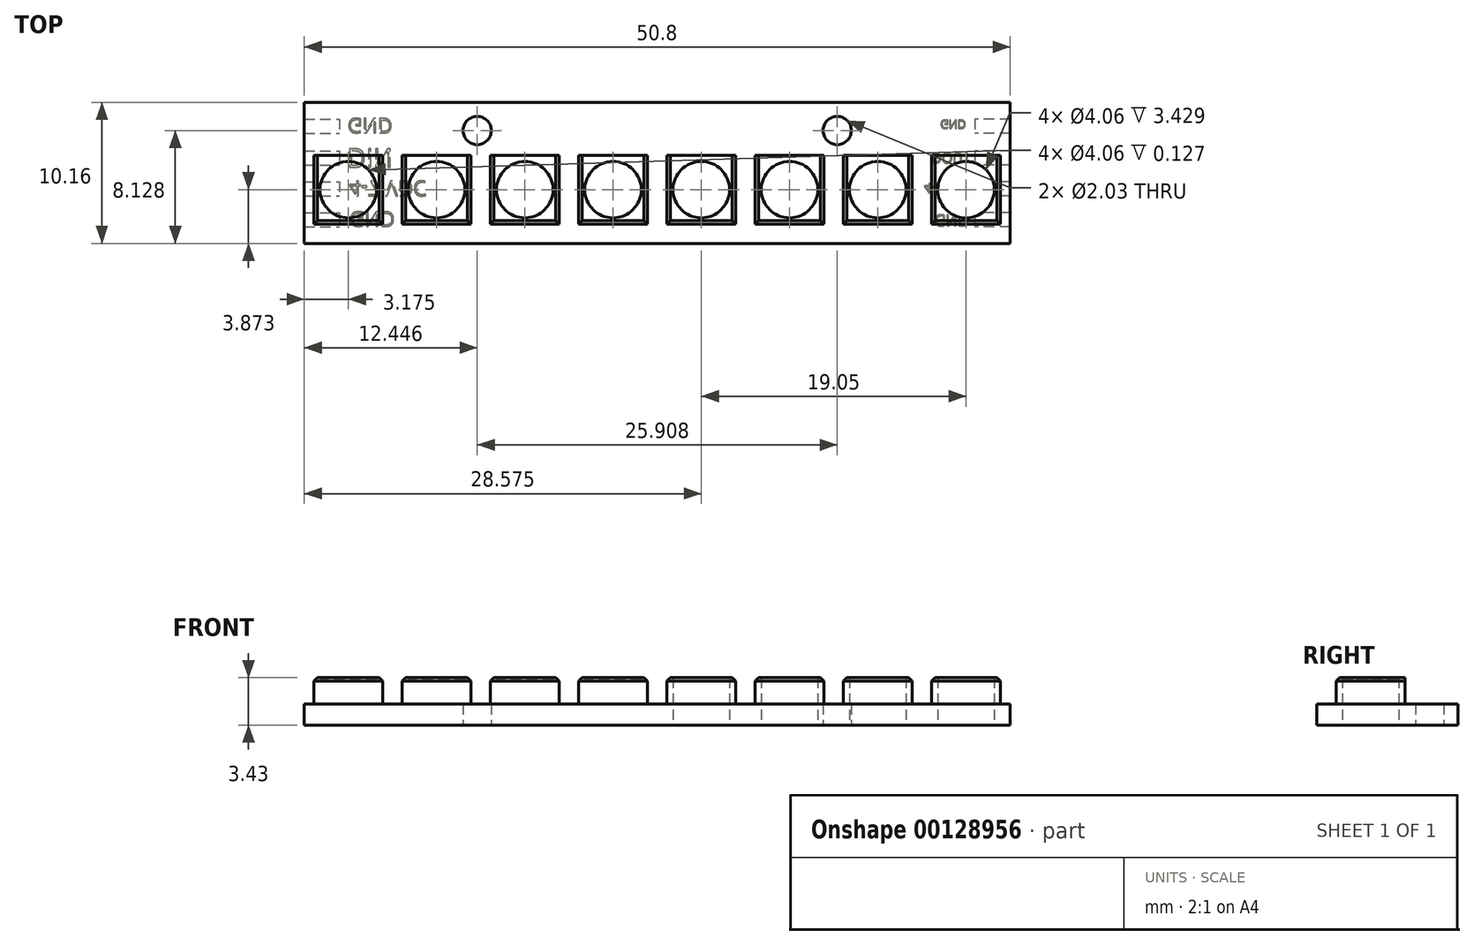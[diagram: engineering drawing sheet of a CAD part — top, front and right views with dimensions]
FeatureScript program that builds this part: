
annotation { "Feature Type Name" : "Feature", "Feature Type Description" : "" }
export const myFeature = defineFeature(function(context is Context, id is Id, definition is map)
    precondition{}
    {
        {
            var Q0;
            Q0=qCreatedBy(makeId("Top.planeOp"),FACE);
            var sketch = newSketch(context, id + "F0", { "sketchPlane" : qUnion([Q0])});
            skLineSegment(sketch, "E0.bottom", {"start": v(25.4, 5.08) * mm, "end": v(-25.4, 5.08) * mm});
            skLineSegment(sketch, "E0.top", {"start": v(25.4, -5.08) * mm, "end": v(-25.4, -5.08) * mm});
            skLineSegment(sketch, "E0.left", {"start": v(25.4, 5.08) * mm, "end": v(25.4, -5.08) * mm});
            skLineSegment(sketch, "E0.right", {"start": v(-25.4, 5.08) * mm, "end": v(-25.4, -5.08) * mm});
            skPoint(sketch, "E0.middle", {"position": v(0, 0) * mm});
            skCircle(sketch, "E1", {"center": v(-12.95, 3.05) * mm, "radius": 1.02 * mm});
            skLineSegment(sketch, "E2", {"start": v(-25.4, 1.27) * mm, "end": v(25.4, 1.27) * mm});
            skLineSegment(sketch, "E3.bottom", {"start": v(-25.4, 1.27) * mm, "end": v(-19.75, 1.27) * mm});
            skLineSegment(sketch, "E3.left", {"start": v(-25.4, 1.27) * mm, "end": v(-25.4, -3.68) * mm});
            skLineSegment(sketch, "E3.right", {"start": v(-19.75, 1.27) * mm, "end": v(-19.75, -3.68) * mm});
            skLineSegment(sketch, "E4.bottom", {"start": v(-18.35, 1.27) * mm, "end": v(-13.4, 1.27) * mm});
            skLineSegment(sketch, "E4.top", {"start": v(-18.35, -3.68) * mm, "end": v(-13.4, -3.68) * mm});
            skLineSegment(sketch, "E4.left", {"start": v(-18.35, 1.27) * mm, "end": v(-18.35, -3.68) * mm});
            skLineSegment(sketch, "E4.right", {"start": v(-13.4, 1.27) * mm, "end": v(-13.4, -3.68) * mm});
            skLineSegment(sketch, "E5.bottom", {"start": v(-12, 1.27) * mm, "end": v(-7.05, 1.27) * mm});
            skLineSegment(sketch, "E5.top", {"start": v(-12, -3.68) * mm, "end": v(-7.05, -3.68) * mm});
            skLineSegment(sketch, "E5.left", {"start": v(-12, 1.27) * mm, "end": v(-12, -3.68) * mm});
            skLineSegment(sketch, "E5.right", {"start": v(-7.05, 1.27) * mm, "end": v(-7.05, -3.68) * mm});
            skPoint(sketch, "E6.oppositeSnap0", {"position": v(-9.53, -3.68) * mm});
            skLineSegment(sketch, "E6.bottom", {"start": v(-5.65, 1.27) * mm, "end": v(-0.7, 1.27) * mm});
            skLineSegment(sketch, "E6.top", {"start": v(-5.65, -3.68) * mm, "end": v(-0.7, -3.68) * mm});
            skLineSegment(sketch, "E6.left", {"start": v(-5.65, 1.27) * mm, "end": v(-5.65, -3.68) * mm});
            skLineSegment(sketch, "E6.right", {"start": v(-0.7, 1.27) * mm, "end": v(-0.7, -3.68) * mm});
            skCircle(sketch, "E7.MirrorC", {"center": v(12.95, 3.05) * mm, "radius": 1.02 * mm});
            skLineSegment(sketch, "E8.MirrorCS", {"start": v(18.35, -3.68) * mm, "end": v(13.4, -3.68) * mm});
            skLineSegment(sketch, "E9.MirrorCS", {"start": v(13.4, 1.27) * mm, "end": v(13.4, -3.68) * mm});
            skLineSegment(sketch, "E10.MirrorCS", {"start": v(18.35, 1.27) * mm, "end": v(18.35, -3.68) * mm});
            skLineSegment(sketch, "E11.MirrorCS", {"start": v(18.35, 1.27) * mm, "end": v(13.4, 1.27) * mm});
            skLineSegment(sketch, "E12.MirrorCS", {"start": v(19.75, 1.27) * mm, "end": v(19.75, -3.68) * mm});
            skLineSegment(sketch, "E13.MirrorCS", {"start": v(25.4, 1.27) * mm, "end": v(19.75, 1.27) * mm});
            skLineSegment(sketch, "E14.MirrorCS", {"start": v(25.4, 1.27) * mm, "end": v(-25.4, 1.27) * mm});
            skLineSegment(sketch, "E15.MirrorCS", {"start": v(12, 1.27) * mm, "end": v(12, -3.68) * mm});
            skLineSegment(sketch, "E16.MirrorCS", {"start": v(12, -3.68) * mm, "end": v(7.05, -3.68) * mm});
            skLineSegment(sketch, "E17.MirrorCS", {"start": v(7.05, 1.27) * mm, "end": v(7.05, -3.68) * mm});
            skLineSegment(sketch, "E18.MirrorCS", {"start": v(5.65, 1.27) * mm, "end": v(5.65, -3.68) * mm});
            skLineSegment(sketch, "E19.MirrorCS", {"start": v(5.65, 1.27) * mm, "end": v(0.7, 1.27) * mm});
            skLineSegment(sketch, "E20.MirrorCS", {"start": v(5.65, -3.68) * mm, "end": v(0.7, -3.68) * mm});
            skLineSegment(sketch, "E21.MirrorCS", {"start": v(0.7, 1.27) * mm, "end": v(0.7, -3.68) * mm});
            skPoint(sketch, "E22.centerSnap0", {"position": v(-15.88, 1.27) * mm});
            skPoint(sketch, "E23.centerSnap0", {"position": v(-9.53, 1.27) * mm});
            skPoint(sketch, "E24.centerSnap0", {"position": v(-3.18, 1.27) * mm});
            skLineSegment(sketch, "E25", {"start": v(-24.7, 1.27) * mm, "end": v(-24.7, -3.68) * mm});
            skLineSegment(sketch, "E26.MirrorCS", {"start": v(24.7, 1.27) * mm, "end": v(24.7, -3.68) * mm});
            skLineSegment(sketch, "E27", {"start": v(24.7, -3.68) * mm, "end": v(19.75, -3.68) * mm});
            skLineSegment(sketch, "E28", {"start": v(-24.7, -3.68) * mm, "end": v(-19.75, -3.68) * mm});
            skCircle(sketch, "E29", {"center": v(-22.23, -1.2) * mm, "radius": 2.03 * mm});
            skCircle(sketch, "E30", {"center": v(-15.88, -1.2) * mm, "radius": 2.03 * mm});
            skCircle(sketch, "E31", {"center": v(-9.53, -1.2) * mm, "radius": 2.03 * mm});
            skCircle(sketch, "E32", {"center": v(-3.18, -1.2) * mm, "radius": 2.03 * mm});
            skCircle(sketch, "E33.MirrorC", {"center": v(3.18, -1.2) * mm, "radius": 2.03 * mm});
            skCircle(sketch, "E34.MirrorC", {"center": v(9.53, -1.2) * mm, "radius": 2.03 * mm});
            skCircle(sketch, "E35.MirrorC", {"center": v(15.88, -1.2) * mm, "radius": 2.03 * mm});
            skCircle(sketch, "E36.MirrorC", {"center": v(22.23, -1.2) * mm, "radius": 2.03 * mm});
            skSolve(sketch);
        }
        {
            var Q0;
            {var subQ15=sQuery(id+"F0.wireOp",EDGE,"E0.bottom");Q0=makeQuery(id+"F0.imprint","IMPRINT",FACE,{"disambiguationData":[TD([[makeQuery(id+"F0.imprint","IMPRINT",EDGE,{"derivedFrom":subQ15}),1.0]])]});}
            var Q1;
            Q1=makeQuery(id+"F0.imprint","IMPRINT",FACE,{"disambiguationData":[TD([[makeQuery(id+"F0.imprint","IMPRINT",EDGE,{"derivedFrom":sQuery(id+"F0.wireOp",EDGE,"E5.top")}),1.0]])]});
            var Q2;
            Q2=makeQuery(id+"F0.imprint","IMPRINT",FACE,{"disambiguationData":[TD([[makeQuery(id+"F0.imprint","IMPRINT",EDGE,{"derivedFrom":sQuery(id+"F0.wireOp",EDGE,"E4.top")}),1.0]])]});
            var Q3;
            Q3=makeQuery(id+"F0.imprint","IMPRINT",FACE,{"disambiguationData":[TD([[makeQuery(id+"F0.imprint","IMPRINT",EDGE,{"derivedFrom":sQuery(id+"F0.wireOp",EDGE,"E3.top")}),1.0]])]});
            var Q4;
            Q4=makeQuery(id+"F0.imprint","IMPRINT",FACE,{"disambiguationData":[TD([[makeQuery(id+"F0.imprint","IMPRINT",EDGE,{"derivedFrom":sQuery(id+"F0.wireOp",EDGE,"E6.top")}),1.0]])]});
            var Q5;
            Q5=makeQuery(id+"F0.imprint","IMPRINT",FACE,{"disambiguationData":[TD([[makeQuery(id+"F0.imprint","IMPRINT",EDGE,{"derivedFrom":sQuery(id+"F0.wireOp",EDGE,"E18.MirrorCS")}),-1.0]])]});
            var Q6;
            {var subQ0=sQuery(id+"F0.wireOp",EDGE,"E15.MirrorCS");Q6=makeQuery(id+"F0.imprint","IMPRINT",FACE,{"disambiguationData":[TD([[makeQuery(id+"F0.imprint","IMPRINT",EDGE,{"derivedFrom":subQ0}),-1.0]])]});}
            var Q7;
            Q7=makeQuery(id+"F0.imprint","IMPRINT",FACE,{"disambiguationData":[TD([[makeQuery(id+"F0.imprint","IMPRINT",EDGE,{"derivedFrom":sQuery(id+"F0.wireOp",EDGE,"E8.MirrorCS")}),-1.0]])]});
            var Q8;
            {var subQ4=sQuery(id+"F0.wireOp",EDGE,"E12.MirrorCS");Q8=makeQuery(id+"F0.imprint","IMPRINT",FACE,{"disambiguationData":[TD([[makeQuery(id+"F0.imprint","IMPRINT",EDGE,{"derivedFrom":subQ4}),1.0]])]});}
            var Q9;
            {var subQ0=sQuery(id+"F0.wireOp",EDGE,"E22");var subQ1=makeQuery(id+"F0.imprint","INTERSECT",VERTEX,{"derivedFrom":[sQuery(id+"F0.wireOp",EDGE,"E4.right"),subQ0]});Q9=makeQuery(id+"F0.imprint","IMPRINT",FACE,{"disambiguationData":[TD([[makeQuery(id+"F0.imprint","IMPRINT",EDGE,{"disambiguationData":[TD([[subQ1,-1.0]])],"derivedFrom":subQ0}),1.0]])]});}
            var Q10;
            {var subQ0=sQuery(id+"F0.wireOp",EDGE,"UNAH1sZw-Ke5a-9nqM-yAOw-CyViDykzE4hE");var subQ1=makeQuery(id+"F0.imprint","INTERSECT",VERTEX,{"derivedFrom":[sQuery(id+"F0.wireOp",EDGE,"E3.right"),subQ0]});Q10=makeQuery(id+"F0.imprint","IMPRINT",FACE,{"disambiguationData":[TD([[makeQuery(id+"F0.imprint","IMPRINT",EDGE,{"disambiguationData":[TD([[subQ1,-1.0]])],"derivedFrom":subQ0}),1.0]])]});}
            var Q11;
            {var subQ1=sQuery(id+"F0.wireOp",EDGE,"E3.left");var subQ3=sQuery(id+"F0.wireOp",EDGE,"UNAH1sZw-Ke5a-9nqM-yAOw-CyViDykzE4hE");var subQ4=makeQuery(id+"F0.imprint","INTERSECT",VERTEX,{"derivedFrom":[subQ1,subQ3]});Q11=makeQuery(id+"F0.imprint","IMPRINT",FACE,{"disambiguationData":[TD([[makeQuery(id+"F0.imprint","IMPRINT",EDGE,{"disambiguationData":[TD([[subQ4,1.0]])],"derivedFrom":subQ3}),-1.0]])]});}
            var Q12;
            {var subQ0=sQuery(id+"F0.wireOp",EDGE,"E14.MirrorCS");var subQ1=sQuery(id+"F0.wireOp",EDGE,"E3.right");var subQ2=makeQuery(id+"F0.imprint","INTERSECT",VERTEX,{"derivedFrom":[subQ1,subQ0]});Q12=makeQuery(id+"F0.imprint","IMPRINT",FACE,{"disambiguationData":[TD([[makeQuery(id+"F0.imprint","IMPRINT",EDGE,{"disambiguationData":[TD([[subQ2,-1.0]])],"derivedFrom":subQ1}),-1.0]])]});}
            var Q13;
            {var subQ0=sQuery(id+"F0.wireOp",EDGE,"E14.MirrorCS");var subQ1=sQuery(id+"F0.wireOp",EDGE,"E4.left");var subQ2=makeQuery(id+"F0.imprint","INTERSECT",VERTEX,{"derivedFrom":[subQ1,subQ0]});Q13=makeQuery(id+"F0.imprint","IMPRINT",FACE,{"disambiguationData":[TD([[makeQuery(id+"F0.imprint","IMPRINT",EDGE,{"disambiguationData":[TD([[subQ2,-1.0]])],"derivedFrom":subQ1}),1.0]])]});}
            var Q14;
            {var subQ52=sQuery(id+"F0.wireOp",EDGE,"E0.top");Q14=makeQuery(id+"F0.imprint","IMPRINT",FACE,{"disambiguationData":[TD([[makeQuery(id+"F0.imprint","IMPRINT",EDGE,{"derivedFrom":subQ52}),-1.0]])]});}
            var Q15;
            {var subQ0=sQuery(id+"F0.wireOp",EDGE,"E14.MirrorCS");var subQ1=sQuery(id+"F0.wireOp",EDGE,"E4.right");var subQ2=makeQuery(id+"F0.imprint","INTERSECT",VERTEX,{"derivedFrom":[subQ1,subQ0]});Q15=makeQuery(id+"F0.imprint","IMPRINT",FACE,{"disambiguationData":[TD([[makeQuery(id+"F0.imprint","IMPRINT",EDGE,{"disambiguationData":[TD([[subQ2,-1.0]])],"derivedFrom":subQ1}),-1.0]])]});}
            var Q16;
            {var subQ0=sQuery(id+"F0.wireOp",EDGE,"E23");var subQ1=makeQuery(id+"F0.imprint","INTERSECT",VERTEX,{"derivedFrom":[sQuery(id+"F0.wireOp",EDGE,"E5.right"),subQ0]});Q16=makeQuery(id+"F0.imprint","IMPRINT",FACE,{"disambiguationData":[TD([[makeQuery(id+"F0.imprint","IMPRINT",EDGE,{"disambiguationData":[TD([[subQ1,-1.0]])],"derivedFrom":subQ0}),1.0]])]});}
            var Q17;
            {var subQ0=sQuery(id+"F0.wireOp",EDGE,"E14.MirrorCS");var subQ1=sQuery(id+"F0.wireOp",EDGE,"E5.left");var subQ2=makeQuery(id+"F0.imprint","INTERSECT",VERTEX,{"derivedFrom":[subQ1,subQ0]});Q17=makeQuery(id+"F0.imprint","IMPRINT",FACE,{"disambiguationData":[TD([[makeQuery(id+"F0.imprint","IMPRINT",EDGE,{"disambiguationData":[TD([[subQ2,-1.0]])],"derivedFrom":subQ1}),1.0]])]});}
            var Q18;
            {var subQ0=sQuery(id+"F0.wireOp",EDGE,"E14.MirrorCS");var subQ1=sQuery(id+"F0.wireOp",EDGE,"E5.right");var subQ2=makeQuery(id+"F0.imprint","INTERSECT",VERTEX,{"derivedFrom":[subQ1,subQ0]});Q18=makeQuery(id+"F0.imprint","IMPRINT",FACE,{"disambiguationData":[TD([[makeQuery(id+"F0.imprint","IMPRINT",EDGE,{"disambiguationData":[TD([[subQ2,-1.0]])],"derivedFrom":subQ1}),-1.0]])]});}
            var Q19;
            {var subQ0=sQuery(id+"F0.wireOp",EDGE,"E24");var subQ1=makeQuery(id+"F0.imprint","INTERSECT",VERTEX,{"derivedFrom":[sQuery(id+"F0.wireOp",EDGE,"E6.right"),subQ0]});Q19=makeQuery(id+"F0.imprint","IMPRINT",FACE,{"disambiguationData":[TD([[makeQuery(id+"F0.imprint","IMPRINT",EDGE,{"disambiguationData":[TD([[subQ1,-1.0]])],"derivedFrom":subQ0}),1.0]])]});}
            var Q20;
            {var subQ0=sQuery(id+"F0.wireOp",EDGE,"E14.MirrorCS");var subQ1=sQuery(id+"F0.wireOp",EDGE,"E6.left");var subQ2=makeQuery(id+"F0.imprint","INTERSECT",VERTEX,{"derivedFrom":[subQ1,subQ0]});Q20=makeQuery(id+"F0.imprint","IMPRINT",FACE,{"disambiguationData":[TD([[makeQuery(id+"F0.imprint","IMPRINT",EDGE,{"disambiguationData":[TD([[subQ2,-1.0]])],"derivedFrom":subQ1}),1.0]])]});}
            var Q21;
            {var subQ0=sQuery(id+"F0.wireOp",EDGE,"E14.MirrorCS");var subQ1=sQuery(id+"F0.wireOp",EDGE,"E6.right");var subQ2=makeQuery(id+"F0.imprint","INTERSECT",VERTEX,{"derivedFrom":[subQ1,subQ0]});Q21=makeQuery(id+"F0.imprint","IMPRINT",FACE,{"disambiguationData":[TD([[makeQuery(id+"F0.imprint","IMPRINT",EDGE,{"disambiguationData":[TD([[subQ2,-1.0]])],"derivedFrom":subQ1}),-1.0]])]});}
            var Q22;
            {var subQ0=sQuery(id+"F0.wireOp",EDGE,"8c9498a9-89d4-41b4-a61f-fcb31b3f8e1a0.MirrorC");var subQ1=makeQuery(id+"F0.imprint","INTERSECT",VERTEX,{"derivedFrom":[sQuery(id+"F0.wireOp",EDGE,"E19.MirrorCS"),subQ0]});Q22=makeQuery(id+"F0.imprint","IMPRINT",FACE,{"disambiguationData":[TD([[makeQuery(id+"F0.imprint","IMPRINT",EDGE,{"disambiguationData":[TD([[subQ1,1.0]])],"derivedFrom":subQ0}),-1.0]])]});}
            var Q23;
            {var subQ0=sQuery(id+"F0.wireOp",EDGE,"724678bf-c758-4b2b-ac49-fb71572171400.MirrorC");var subQ1=makeQuery(id+"F0.imprint","INTERSECT",VERTEX,{"derivedFrom":[sQuery(id+"F0.wireOp",EDGE,"E14.MirrorCS"),subQ0]});Q23=makeQuery(id+"F0.imprint","IMPRINT",FACE,{"disambiguationData":[TD([[makeQuery(id+"F0.imprint","IMPRINT",EDGE,{"disambiguationData":[TD([[subQ1,1.0]])],"derivedFrom":subQ0}),-1.0]])]});}
            var Q24;
            {var subQ0=sQuery(id+"F0.wireOp",EDGE,"96d1a491-8e30-4fa4-92a3-82973c83916c0.MirrorC");var subQ1=makeQuery(id+"F0.imprint","INTERSECT",VERTEX,{"derivedFrom":[sQuery(id+"F0.wireOp",EDGE,"E9.MirrorCS"),subQ0]});Q24=makeQuery(id+"F0.imprint","IMPRINT",FACE,{"disambiguationData":[TD([[makeQuery(id+"F0.imprint","IMPRINT",EDGE,{"disambiguationData":[TD([[subQ1,-1.0]])],"derivedFrom":subQ0}),-1.0]])]});}
            var Q25;
            {var subQ0=sQuery(id+"F0.wireOp",EDGE,"E14.MirrorCS");var subQ1=sQuery(id+"F0.wireOp",EDGE,"E9.MirrorCS");var subQ2=makeQuery(id+"F0.imprint","INTERSECT",VERTEX,{"derivedFrom":[subQ1,subQ0]});Q25=makeQuery(id+"F0.imprint","IMPRINT",FACE,{"disambiguationData":[TD([[makeQuery(id+"F0.imprint","IMPRINT",EDGE,{"disambiguationData":[TD([[subQ2,-1.0]])],"derivedFrom":subQ1}),1.0]])]});}
            var Q26;
            {var subQ0=sQuery(id+"F0.wireOp",EDGE,"E14.MirrorCS");var subQ1=sQuery(id+"F0.wireOp",EDGE,"E10.MirrorCS");var subQ2=makeQuery(id+"F0.imprint","INTERSECT",VERTEX,{"derivedFrom":[subQ1,subQ0]});Q26=makeQuery(id+"F0.imprint","IMPRINT",FACE,{"disambiguationData":[TD([[makeQuery(id+"F0.imprint","IMPRINT",EDGE,{"disambiguationData":[TD([[subQ2,-1.0]])],"derivedFrom":subQ1}),-1.0]])]});}
            var Q27;
            {var subQ0=sQuery(id+"F0.wireOp",EDGE,"dc3a0b8c-c6c2-4147-8545-72a2fc5a206e0.MirrorC");var subQ1=makeQuery(id+"F0.imprint","INTERSECT",VERTEX,{"derivedFrom":[sQuery(id+"F0.wireOp",EDGE,"E12.MirrorCS"),subQ0]});Q27=makeQuery(id+"F0.imprint","IMPRINT",FACE,{"disambiguationData":[TD([[makeQuery(id+"F0.imprint","IMPRINT",EDGE,{"disambiguationData":[TD([[subQ1,-1.0]])],"derivedFrom":subQ0}),-1.0]])]});}
            var Q28;
            {var subQ0=sQuery(id+"F0.wireOp",EDGE,"4b35c337-2ec3-4570-835e-5a8300de2a6e0.MirrorCS");var subQ1=sQuery(id+"F0.wireOp",EDGE,"E0.left");var subQ2=makeQuery(id+"F0.imprint","INTERSECT",VERTEX,{"derivedFrom":[subQ1,subQ0]});Q28=makeQuery(id+"F0.imprint","IMPRINT",FACE,{"disambiguationData":[TD([[makeQuery(id+"F0.imprint","IMPRINT",EDGE,{"disambiguationData":[TD([[subQ2,1.0]])],"derivedFrom":subQ1}),-1.0]])]});}
            var Q29;
            {var subQ0=sQuery(id+"F0.wireOp",EDGE,"E14.MirrorCS");var subQ1=sQuery(id+"F0.wireOp",EDGE,"E0.left");var subQ2=makeQuery(id+"F0.imprint","INTERSECT",VERTEX,{"derivedFrom":[subQ1,subQ0]});Q29=makeQuery(id+"F0.imprint","IMPRINT",FACE,{"disambiguationData":[TD([[makeQuery(id+"F0.imprint","IMPRINT",EDGE,{"disambiguationData":[TD([[subQ2,-1.0]])],"derivedFrom":subQ1}),-1.0]])]});}
            var Q30;
            {var subQ0=sQuery(id+"F0.wireOp",EDGE,"E17.MirrorCS");var subQ1=sQuery(id+"F0.wireOp",EDGE,"E14.MirrorCS");var subQ2=makeQuery(id+"F0.imprint","INTERSECT",VERTEX,{"derivedFrom":[subQ1,subQ0]});Q30=makeQuery(id+"F0.imprint","IMPRINT",FACE,{"disambiguationData":[TD([[makeQuery(id+"F0.imprint","IMPRINT",EDGE,{"disambiguationData":[TD([[subQ2,1.0]])],"derivedFrom":subQ1}),1.0]])]});}
            var Q31;
            {var subQ0=sQuery(id+"F0.wireOp",EDGE,"E17.MirrorCS");var subQ1=sQuery(id+"F0.wireOp",EDGE,"E16.MirrorCS");var subQ2=makeQuery(id+"F0.imprint","INTERSECT",VERTEX,{"derivedFrom":[subQ1,subQ0]});Q31=makeQuery(id+"F0.imprint","IMPRINT",FACE,{"disambiguationData":[TD([[makeQuery(id+"F0.imprint","IMPRINT",EDGE,{"disambiguationData":[TD([[subQ2,1.0]])],"derivedFrom":subQ1}),-1.0]])]});}
            var Q32;
            {var subQ0=sQuery(id+"F0.wireOp",EDGE,"E21.MirrorCS");var subQ1=sQuery(id+"F0.wireOp",EDGE,"E20.MirrorCS");var subQ2=makeQuery(id+"F0.imprint","INTERSECT",VERTEX,{"derivedFrom":[subQ1,subQ0]});Q32=makeQuery(id+"F0.imprint","IMPRINT",FACE,{"disambiguationData":[TD([[makeQuery(id+"F0.imprint","IMPRINT",EDGE,{"disambiguationData":[TD([[subQ2,1.0]])],"derivedFrom":subQ1}),-1.0]])]});}
            var Q33;
            {var subQ1=sQuery(id+"F0.wireOp",EDGE,"E19.MirrorCS");var subQ3=sQuery(id+"F0.wireOp",EDGE,"8c9498a9-89d4-41b4-a61f-fcb31b3f8e1a0.MirrorC");var subQ4=makeQuery(id+"F0.imprint","INTERSECT",VERTEX,{"derivedFrom":[subQ1,subQ3]});Q33=makeQuery(id+"F0.imprint","IMPRINT",FACE,{"disambiguationData":[TD([[makeQuery(id+"F0.imprint","IMPRINT",EDGE,{"disambiguationData":[TD([[subQ4,1.0]])],"derivedFrom":subQ3}),1.0]])]});}
            var Q34;
            {var subQ0=sQuery(id+"F0.wireOp",EDGE,"E28");var subQ1=sQuery(id+"F0.wireOp",EDGE,"E3.right");var subQ2=makeQuery(id+"F0.imprint","INTERSECT",VERTEX,{"derivedFrom":[subQ1,subQ0]});Q34=makeQuery(id+"F0.imprint","IMPRINT",FACE,{"disambiguationData":[TD([[makeQuery(id+"F0.imprint","IMPRINT",EDGE,{"disambiguationData":[TD([[subQ2,1.0]])],"derivedFrom":subQ1}),-1.0]])]});}
            var Q35;
            {var subQ0=sQuery(id+"F0.wireOp",EDGE,"1PWdEQUw-wEJ5-cKNr-TaBA-1jAVnnhFksSZ");var subQ1=makeQuery(id+"F0.imprint","INTERSECT",VERTEX,{"derivedFrom":[sQuery(id+"F0.wireOp",EDGE,"E3.right"),subQ0]});Q35=makeQuery(id+"F0.imprint","IMPRINT",FACE,{"disambiguationData":[TD([[makeQuery(id+"F0.imprint","IMPRINT",EDGE,{"disambiguationData":[TD([[subQ1,-1.0]])],"derivedFrom":subQ0}),1.0]])]});}
            var Q36;
            {var subQ0=sQuery(id+"F0.wireOp",EDGE,"E25");var subQ1=sQuery(id+"F0.wireOp",EDGE,"E14.MirrorCS");var subQ2=makeQuery(id+"F0.imprint","INTERSECT",VERTEX,{"derivedFrom":[subQ1,subQ0]});Q36=makeQuery(id+"F0.imprint","IMPRINT",FACE,{"disambiguationData":[TD([[makeQuery(id+"F0.imprint","IMPRINT",EDGE,{"disambiguationData":[TD([[subQ2,1.0]])],"derivedFrom":subQ1}),1.0]])]});}
            var Q37;
            {var subQ0=sQuery(id+"F0.wireOp",EDGE,"E28");var subQ1=sQuery(id+"F0.wireOp",EDGE,"E25");var subQ2=makeQuery(id+"F0.imprint","INTERSECT",VERTEX,{"derivedFrom":[subQ1,subQ0]});Q37=makeQuery(id+"F0.imprint","IMPRINT",FACE,{"disambiguationData":[TD([[makeQuery(id+"F0.imprint","IMPRINT",EDGE,{"disambiguationData":[TD([[subQ2,1.0]])],"derivedFrom":subQ1}),1.0]])]});}
            var Q38;
            {var subQ0=sQuery(id+"F0.wireOp",EDGE,"3694e821-6fd0-43f0-b6cd-c99c7b0efe270.MirrorC");var subQ1=makeQuery(id+"F0.imprint","INTERSECT",VERTEX,{"derivedFrom":[sQuery(id+"F0.wireOp",EDGE,"E12.MirrorCS"),subQ0]});Q38=makeQuery(id+"F0.imprint","IMPRINT",FACE,{"disambiguationData":[TD([[makeQuery(id+"F0.imprint","IMPRINT",EDGE,{"disambiguationData":[TD([[subQ1,-1.0]])],"derivedFrom":subQ0}),-1.0]])]});}
            var Q39;
            {var subQ0=sQuery(id+"F0.wireOp",EDGE,"E26.MirrorCS");var subQ1=sQuery(id+"F0.wireOp",EDGE,"E14.MirrorCS");var subQ2=makeQuery(id+"F0.imprint","INTERSECT",VERTEX,{"derivedFrom":[subQ1,subQ0]});Q39=makeQuery(id+"F0.imprint","IMPRINT",FACE,{"disambiguationData":[TD([[makeQuery(id+"F0.imprint","IMPRINT",EDGE,{"disambiguationData":[TD([[subQ2,-1.0]])],"derivedFrom":subQ1}),1.0]])]});}
            var Q40;
            {var subQ0=sQuery(id+"F0.wireOp",EDGE,"E26.MirrorCS");var subQ1=sQuery(id+"F0.wireOp",EDGE,"3694e821-6fd0-43f0-b6cd-c99c7b0efe270.MirrorC");var subQ2=makeQuery(id+"F0.imprint","INTERSECT",VERTEX,{"derivedFrom":[subQ1,subQ0]});Q40=makeQuery(id+"F0.imprint","IMPRINT",FACE,{"disambiguationData":[TD([[makeQuery(id+"F0.imprint","IMPRINT",EDGE,{"disambiguationData":[TD([[subQ2,-1.0]])],"derivedFrom":subQ1}),1.0]])]});}
            var Q41;
            Q41=makeQuery(id+"F0.imprint","IMPRINT",FACE,{"disambiguationData":[TD([[makeQuery(id+"F0.imprint","IMPRINT",EDGE,{"derivedFrom":sQuery(id+"F0.wireOp",EDGE,"E29")}),1.0]])]});
            var Q42;
            Q42=makeQuery(id+"F0.imprint","IMPRINT",FACE,{"disambiguationData":[TD([[makeQuery(id+"F0.imprint","IMPRINT",EDGE,{"derivedFrom":sQuery(id+"F0.wireOp",EDGE,"E30")}),1.0]])]});
            var Q43;
            Q43=makeQuery(id+"F0.imprint","IMPRINT",FACE,{"disambiguationData":[TD([[makeQuery(id+"F0.imprint","IMPRINT",EDGE,{"derivedFrom":sQuery(id+"F0.wireOp",EDGE,"E31")}),1.0]])]});
            var Q44;
            Q44=makeQuery(id+"F0.imprint","IMPRINT",FACE,{"disambiguationData":[TD([[makeQuery(id+"F0.imprint","IMPRINT",EDGE,{"derivedFrom":sQuery(id+"F0.wireOp",EDGE,"E33.MirrorC")}),-1.0]])]});
            var Q45;
            Q45=makeQuery(id+"F0.imprint","IMPRINT",FACE,{"disambiguationData":[TD([[makeQuery(id+"F0.imprint","IMPRINT",EDGE,{"derivedFrom":sQuery(id+"F0.wireOp",EDGE,"E34.MirrorC")}),-1.0]])]});
            var Q46;
            Q46=makeQuery(id+"F0.imprint","IMPRINT",FACE,{"disambiguationData":[TD([[makeQuery(id+"F0.imprint","IMPRINT",EDGE,{"derivedFrom":sQuery(id+"F0.wireOp",EDGE,"E32")}),1.0]])]});
            var Q47;
            Q47=makeQuery(id+"F0.imprint","IMPRINT",FACE,{"disambiguationData":[TD([[makeQuery(id+"F0.imprint","IMPRINT",EDGE,{"derivedFrom":sQuery(id+"F0.wireOp",EDGE,"E35.MirrorC")}),-1.0]])]});
            var Q48;
            Q48=makeQuery(id+"F0.imprint","IMPRINT",FACE,{"disambiguationData":[TD([[makeQuery(id+"F0.imprint","IMPRINT",EDGE,{"derivedFrom":sQuery(id+"F0.wireOp",EDGE,"E36.MirrorC")}),-1.0]])]});
            extrude(context, id + "F1", {"entities" : qUnion([Q0, Q1, Q2, Q3, Q4, Q5, Q6, Q7, Q8, Q9, Q10, Q11, Q12, Q13, Q14, Q15, Q16, Q17, Q18, Q19, Q20, Q21, Q22, Q23, Q24, Q25, Q26, Q27, Q28, Q29, Q30, Q31, Q32, Q33, Q34, Q35, Q36, Q37, Q38, Q39, Q40, Q41, Q42, Q43, Q44, Q45, Q46, Q47, Q48]), "depth" : 1.52 * mm, "symmetric" : true});
        }
        {
            var Q0;
            Q0=makeQuery(id+"F1.opExtrude","CAP_FACE",FACE,{"disambiguationData":[OSD([sQuery(id+"F0.wireOp",EDGE,"E0.bottom"),sQuery(id+"F0.wireOp",EDGE,"E0.top"),sQuery(id+"F0.wireOp",EDGE,"E0.left"),sQuery(id+"F0.wireOp",EDGE,"E0.right"),sQuery(id+"F0.wireOp",EDGE,"E1"),sQuery(id+"F0.wireOp",EDGE,"E3.left"),sQuery(id+"F0.wireOp",EDGE,"E7.MirrorC")])],"isStart":true});
            var sketch = newSketch(context, id + "F2", { "sketchPlane" : qUnion([Q0])});
            skLineSegment(sketch, "E37.bottom", {"start": v(25.4, -3.87) * mm, "end": v(22.86, -3.87) * mm});
            skLineSegment(sketch, "E37.top", {"start": v(25.4, -2.86) * mm, "end": v(22.86, -2.86) * mm});
            skLineSegment(sketch, "E37.left", {"start": v(25.4, -3.87) * mm, "end": v(25.4, -2.86) * mm});
            skLineSegment(sketch, "E37.right", {"start": v(22.86, -3.87) * mm, "end": v(22.86, -2.86) * mm});
            skLineSegment(sketch, "E38.bottom", {"start": v(25.4, -1.59) * mm, "end": v(22.86, -1.59) * mm});
            skLineSegment(sketch, "E38.top", {"start": v(25.4, -0.57) * mm, "end": v(22.86, -0.57) * mm});
            skLineSegment(sketch, "E38.left", {"start": v(25.4, -1.59) * mm, "end": v(25.4, -0.57) * mm});
            skLineSegment(sketch, "E38.right", {"start": v(22.86, -1.59) * mm, "end": v(22.86, -0.57) * mm});
            skLineSegment(sketch, "E39.bottom", {"start": v(25.4, 0.64) * mm, "end": v(22.86, 0.64) * mm});
            skLineSegment(sketch, "E39.top", {"start": v(25.4, 1.65) * mm, "end": v(22.86, 1.65) * mm});
            skLineSegment(sketch, "E39.left", {"start": v(25.4, 0.64) * mm, "end": v(25.4, 1.65) * mm});
            skLineSegment(sketch, "E39.right", {"start": v(22.86, 0.64) * mm, "end": v(22.86, 1.65) * mm});
            skLineSegment(sketch, "E40.bottom", {"start": v(25.4, 2.86) * mm, "end": v(22.86, 2.86) * mm});
            skLineSegment(sketch, "E40.top", {"start": v(25.4, 3.87) * mm, "end": v(22.86, 3.87) * mm});
            skLineSegment(sketch, "E40.left", {"start": v(25.4, 2.86) * mm, "end": v(25.4, 3.87) * mm});
            skLineSegment(sketch, "E40.right", {"start": v(22.86, 2.86) * mm, "end": v(22.86, 3.87) * mm});
            skLineSegment(sketch, "E41.MirrorCS", {"start": v(22.86, -3.87) * mm, "end": v(22.86, -4.89) * mm});
            skLineSegment(sketch, "E42.MirrorCS", {"start": v(-25.4, -3.87) * mm, "end": v(-22.86, -3.87) * mm});
            skLineSegment(sketch, "E43.MirrorCS", {"start": v(-22.86, -3.87) * mm, "end": v(-22.86, -2.86) * mm});
            skLineSegment(sketch, "E44.MirrorCS", {"start": v(-25.4, -2.86) * mm, "end": v(-22.86, -2.86) * mm});
            skLineSegment(sketch, "E45.MirrorCS", {"start": v(-25.4, -1.59) * mm, "end": v(-22.86, -1.59) * mm});
            skLineSegment(sketch, "E46.MirrorCS", {"start": v(-22.86, -1.59) * mm, "end": v(-22.86, -0.57) * mm});
            skLineSegment(sketch, "E47.MirrorCS", {"start": v(-25.4, -0.57) * mm, "end": v(-22.86, -0.57) * mm});
            skLineSegment(sketch, "E48.MirrorCS", {"start": v(-25.4, 0.64) * mm, "end": v(-22.86, 0.64) * mm});
            skLineSegment(sketch, "E49.MirrorCS", {"start": v(-22.86, 0.64) * mm, "end": v(-22.86, 1.65) * mm});
            skLineSegment(sketch, "E50.MirrorCS", {"start": v(-25.4, 1.65) * mm, "end": v(-22.86, 1.65) * mm});
            skLineSegment(sketch, "E51.MirrorCS", {"start": v(-22.86, 2.86) * mm, "end": v(-22.86, 3.87) * mm});
            skLineSegment(sketch, "E52.MirrorCS", {"start": v(-25.4, 2.86) * mm, "end": v(-22.86, 2.86) * mm});
            skLineSegment(sketch, "E53.MirrorCS", {"start": v(-25.4, 3.87) * mm, "end": v(-22.86, 3.87) * mm});
            skText(sketch, "E54", { "text": "GND", "fontName": "OpenSans-Regular.ttf"});
            skText(sketch, "E55", { "text": "DOUT", "fontName": "OpenSans-Regular.ttf"});
            skText(sketch, "E56", { "text": "4-7 VDC", "fontName": "OpenSans-Regular.ttf"});
            skText(sketch, "E57", { "text": "GND", "fontName": "OpenSans-Regular.ttf"});
            skText(sketch, "E58", { "text": "GND\n", "fontName": "OpenSans-Regular.ttf"});
            skText(sketch, "E59", { "text": "DIN", "fontName": "OpenSans-Regular.ttf"});
            skText(sketch, "E60", { "text": "4-7 VDC", "fontName": "OpenSans-Regular.ttf"});
            skText(sketch, "E61", { "text": "GND", "fontName": "OpenSans-Regular.ttf"});
            const initialGuessF2  = {"E54": [0.02037, -0.0038, 1, 0, 0.0006], "E55": [0.01973, -0.00143, 1, 0, 0.00073], "E56": [0.01922, 0.00078, 1, 0, 0.00065], "E57": [0.01995, 0.00303, 1, 0, 0.0008], "E58": [-0.02228, -0.00392, 1, 0, 0.00105], "E59": [-0.02233, -0.00174, 1, 0, 0.00135], "E60": [-0.02218, 0.00058, 1, 0, 0.00109], "E61": [-0.02214, 0.0028, 1, 0, 0.00106]};
            skSetInitialGuess(sketch, initialGuessF2);
            skSolve(sketch);
        }
        {
            var Q0;
            Q0 = qSketchRegion(id + "F2", true);
            var Q1;
            Q1=makeQuery(id+"F2.imprint","IMPRINT",FACE,{"disambiguationData":[TD([[makeQuery(id+"F2.imprint","IMPRINT",EDGE,{"derivedFrom":sQuery(id+"F2.wireOp",EDGE,"E51.MirrorCS")}),1.0]])]});
            var Q2;
            {var subQ0=sQuery(id+"F2.wireOp",EDGE,"E48.MirrorCS");Q2=makeQuery(id+"F2.imprint","IMPRINT",FACE,{"disambiguationData":[TD([[makeQuery(id+"F2.imprint","IMPRINT",EDGE,{"derivedFrom":subQ0}),1.0]])]});}
            var Q3;
            {var subQ0=sQuery(id+"F2.wireOp",EDGE,"E45.MirrorCS");Q3=makeQuery(id+"F2.imprint","IMPRINT",FACE,{"disambiguationData":[TD([[makeQuery(id+"F2.imprint","IMPRINT",EDGE,{"derivedFrom":subQ0}),1.0]])]});}
            var Q4;
            {var subQ0=sQuery(id+"F2.wireOp",EDGE,"E42.MirrorCS");Q4=makeQuery(id+"F2.imprint","IMPRINT",FACE,{"disambiguationData":[TD([[makeQuery(id+"F2.imprint","IMPRINT",EDGE,{"derivedFrom":subQ0}),1.0]])]});}
            extrude(context, id + "F3", {"entities" : qUnion([Q0, Q1, Q2, Q3, Q4]), "operationType" : NewBodyOperationType.REMOVE, "oppositeDirection" : true, "depth" : 0.01 * mm});
        }
        {
            var Q0;
            {var subQ0=sQuery(id+"F0.wireOp",EDGE,"E26.MirrorCS");var subQ1=sQuery(id+"F0.wireOp",EDGE,"E14.MirrorCS");var subQ2=makeQuery(id+"F0.imprint","INTERSECT",VERTEX,{"derivedFrom":[subQ1,subQ0]});Q0=makeQuery(id+"F0.imprint","IMPRINT",FACE,{"disambiguationData":[TD([[makeQuery(id+"F0.imprint","IMPRINT",EDGE,{"disambiguationData":[TD([[subQ2,-1.0]])],"derivedFrom":subQ1}),1.0]])]});}
            var Q1;
            {var subQ0=sQuery(id+"F0.wireOp",EDGE,"E26.MirrorCS");var subQ1=sQuery(id+"F0.wireOp",EDGE,"3694e821-6fd0-43f0-b6cd-c99c7b0efe270.MirrorC");var subQ2=makeQuery(id+"F0.imprint","INTERSECT",VERTEX,{"derivedFrom":[subQ1,subQ0]});Q1=makeQuery(id+"F0.imprint","IMPRINT",FACE,{"disambiguationData":[TD([[makeQuery(id+"F0.imprint","IMPRINT",EDGE,{"disambiguationData":[TD([[subQ2,-1.0]])],"derivedFrom":subQ1}),1.0]])]});}
            var Q2;
            {var subQ0=sQuery(id+"F0.wireOp",EDGE,"E27");var subQ1=sQuery(id+"F0.wireOp",EDGE,"E12.MirrorCS");var subQ2=makeQuery(id+"F0.imprint","INTERSECT",VERTEX,{"derivedFrom":[subQ1,subQ0]});Q2=makeQuery(id+"F0.imprint","IMPRINT",FACE,{"disambiguationData":[TD([[makeQuery(id+"F0.imprint","IMPRINT",EDGE,{"disambiguationData":[TD([[subQ2,1.0]])],"derivedFrom":subQ1}),1.0]])]});}
            var Q3;
            {var subQ0=sQuery(id+"F0.wireOp",EDGE,"E14.MirrorCS");var subQ1=sQuery(id+"F0.wireOp",EDGE,"E12.MirrorCS");var subQ2=makeQuery(id+"F0.imprint","INTERSECT",VERTEX,{"derivedFrom":[subQ1,subQ0]});Q3=makeQuery(id+"F0.imprint","IMPRINT",FACE,{"disambiguationData":[TD([[makeQuery(id+"F0.imprint","IMPRINT",EDGE,{"disambiguationData":[TD([[subQ2,-1.0]])],"derivedFrom":subQ1}),1.0]])]});}
            var Q4;
            {var subQ0=sQuery(id+"F0.wireOp",EDGE,"E14.MirrorCS");var subQ1=sQuery(id+"F0.wireOp",EDGE,"E10.MirrorCS");var subQ2=makeQuery(id+"F0.imprint","INTERSECT",VERTEX,{"derivedFrom":[subQ1,subQ0]});Q4=makeQuery(id+"F0.imprint","IMPRINT",FACE,{"disambiguationData":[TD([[makeQuery(id+"F0.imprint","IMPRINT",EDGE,{"disambiguationData":[TD([[subQ2,-1.0]])],"derivedFrom":subQ1}),-1.0]])]});}
            var Q5;
            {var subQ0=sQuery(id+"F0.wireOp",EDGE,"E10.MirrorCS");var subQ1=sQuery(id+"F0.wireOp",EDGE,"E8.MirrorCS");var subQ2=makeQuery(id+"F0.imprint","INTERSECT",VERTEX,{"derivedFrom":[subQ1,subQ0]});Q5=makeQuery(id+"F0.imprint","IMPRINT",FACE,{"disambiguationData":[TD([[makeQuery(id+"F0.imprint","IMPRINT",EDGE,{"disambiguationData":[TD([[subQ2,-1.0]])],"derivedFrom":subQ1}),-1.0]])]});}
            var Q6;
            {var subQ0=sQuery(id+"F0.wireOp",EDGE,"E9.MirrorCS");var subQ1=sQuery(id+"F0.wireOp",EDGE,"E8.MirrorCS");var subQ2=makeQuery(id+"F0.imprint","INTERSECT",VERTEX,{"derivedFrom":[subQ1,subQ0]});Q6=makeQuery(id+"F0.imprint","IMPRINT",FACE,{"disambiguationData":[TD([[makeQuery(id+"F0.imprint","IMPRINT",EDGE,{"disambiguationData":[TD([[subQ2,1.0]])],"derivedFrom":subQ1}),-1.0]])]});}
            var Q7;
            {var subQ0=sQuery(id+"F0.wireOp",EDGE,"E14.MirrorCS");var subQ1=sQuery(id+"F0.wireOp",EDGE,"E9.MirrorCS");var subQ2=makeQuery(id+"F0.imprint","INTERSECT",VERTEX,{"derivedFrom":[subQ1,subQ0]});Q7=makeQuery(id+"F0.imprint","IMPRINT",FACE,{"disambiguationData":[TD([[makeQuery(id+"F0.imprint","IMPRINT",EDGE,{"disambiguationData":[TD([[subQ2,-1.0]])],"derivedFrom":subQ1}),1.0]])]});}
            var Q8;
            {var subQ0=sQuery(id+"F0.wireOp",EDGE,"E15.MirrorCS");var subQ1=sQuery(id+"F0.wireOp",EDGE,"E14.MirrorCS");var subQ2=makeQuery(id+"F0.imprint","INTERSECT",VERTEX,{"derivedFrom":[subQ1,subQ0]});Q8=makeQuery(id+"F0.imprint","IMPRINT",FACE,{"disambiguationData":[TD([[makeQuery(id+"F0.imprint","IMPRINT",EDGE,{"disambiguationData":[TD([[subQ2,-1.0]])],"derivedFrom":subQ1}),1.0]])]});}
            var Q9;
            {var subQ0=sQuery(id+"F0.wireOp",EDGE,"E16.MirrorCS");var subQ1=sQuery(id+"F0.wireOp",EDGE,"E15.MirrorCS");var subQ2=makeQuery(id+"F0.imprint","INTERSECT",VERTEX,{"derivedFrom":[subQ1,subQ0]});Q9=makeQuery(id+"F0.imprint","IMPRINT",FACE,{"disambiguationData":[TD([[makeQuery(id+"F0.imprint","IMPRINT",EDGE,{"disambiguationData":[TD([[subQ2,1.0]])],"derivedFrom":subQ1}),-1.0]])]});}
            var Q10;
            {var subQ0=sQuery(id+"F0.wireOp",EDGE,"E17.MirrorCS");var subQ1=sQuery(id+"F0.wireOp",EDGE,"E14.MirrorCS");var subQ2=makeQuery(id+"F0.imprint","INTERSECT",VERTEX,{"derivedFrom":[subQ1,subQ0]});Q10=makeQuery(id+"F0.imprint","IMPRINT",FACE,{"disambiguationData":[TD([[makeQuery(id+"F0.imprint","IMPRINT",EDGE,{"disambiguationData":[TD([[subQ2,1.0]])],"derivedFrom":subQ1}),1.0]])]});}
            var Q11;
            {var subQ0=sQuery(id+"F0.wireOp",EDGE,"E17.MirrorCS");var subQ1=sQuery(id+"F0.wireOp",EDGE,"E16.MirrorCS");var subQ2=makeQuery(id+"F0.imprint","INTERSECT",VERTEX,{"derivedFrom":[subQ1,subQ0]});Q11=makeQuery(id+"F0.imprint","IMPRINT",FACE,{"disambiguationData":[TD([[makeQuery(id+"F0.imprint","IMPRINT",EDGE,{"disambiguationData":[TD([[subQ2,1.0]])],"derivedFrom":subQ1}),-1.0]])]});}
            var Q12;
            {var subQ0=sQuery(id+"F0.wireOp",EDGE,"E20.MirrorCS");var subQ1=sQuery(id+"F0.wireOp",EDGE,"E18.MirrorCS");var subQ2=makeQuery(id+"F0.imprint","INTERSECT",VERTEX,{"derivedFrom":[subQ1,subQ0]});Q12=makeQuery(id+"F0.imprint","IMPRINT",FACE,{"disambiguationData":[TD([[makeQuery(id+"F0.imprint","IMPRINT",EDGE,{"disambiguationData":[TD([[subQ2,1.0]])],"derivedFrom":subQ1}),-1.0]])]});}
            var Q13;
            {var subQ1=sQuery(id+"F0.wireOp",EDGE,"E18.MirrorCS");var subQ3=sQuery(id+"F0.wireOp",EDGE,"8c9498a9-89d4-41b4-a61f-fcb31b3f8e1a0.MirrorC");var subQ4=makeQuery(id+"F0.imprint","INTERSECT",VERTEX,{"derivedFrom":[subQ1,subQ3]});Q13=makeQuery(id+"F0.imprint","IMPRINT",FACE,{"disambiguationData":[TD([[makeQuery(id+"F0.imprint","IMPRINT",EDGE,{"disambiguationData":[TD([[subQ4,1.0]])],"derivedFrom":subQ3}),1.0]])]});}
            var Q14;
            {var subQ1=sQuery(id+"F0.wireOp",EDGE,"E19.MirrorCS");var subQ3=sQuery(id+"F0.wireOp",EDGE,"8c9498a9-89d4-41b4-a61f-fcb31b3f8e1a0.MirrorC");var subQ4=makeQuery(id+"F0.imprint","INTERSECT",VERTEX,{"derivedFrom":[subQ1,subQ3]});Q14=makeQuery(id+"F0.imprint","IMPRINT",FACE,{"disambiguationData":[TD([[makeQuery(id+"F0.imprint","IMPRINT",EDGE,{"disambiguationData":[TD([[subQ4,1.0]])],"derivedFrom":subQ3}),1.0]])]});}
            var Q15;
            {var subQ0=sQuery(id+"F0.wireOp",EDGE,"E21.MirrorCS");var subQ1=sQuery(id+"F0.wireOp",EDGE,"E20.MirrorCS");var subQ2=makeQuery(id+"F0.imprint","INTERSECT",VERTEX,{"derivedFrom":[subQ1,subQ0]});Q15=makeQuery(id+"F0.imprint","IMPRINT",FACE,{"disambiguationData":[TD([[makeQuery(id+"F0.imprint","IMPRINT",EDGE,{"disambiguationData":[TD([[subQ2,1.0]])],"derivedFrom":subQ1}),-1.0]])]});}
            var Q16;
            {var subQ0=sQuery(id+"F0.wireOp",EDGE,"E14.MirrorCS");var subQ1=sQuery(id+"F0.wireOp",EDGE,"E6.right");var subQ2=makeQuery(id+"F0.imprint","INTERSECT",VERTEX,{"derivedFrom":[subQ1,subQ0]});Q16=makeQuery(id+"F0.imprint","IMPRINT",FACE,{"disambiguationData":[TD([[makeQuery(id+"F0.imprint","IMPRINT",EDGE,{"disambiguationData":[TD([[subQ2,-1.0]])],"derivedFrom":subQ1}),-1.0]])]});}
            var Q17;
            {var subQ0=sQuery(id+"F0.wireOp",EDGE,"E6.right");var subQ1=sQuery(id+"F0.wireOp",EDGE,"E6.top");var subQ2=makeQuery(id+"F0.imprint","INTERSECT",VERTEX,{"derivedFrom":[subQ1,subQ0]});Q17=makeQuery(id+"F0.imprint","IMPRINT",FACE,{"disambiguationData":[TD([[makeQuery(id+"F0.imprint","IMPRINT",EDGE,{"disambiguationData":[TD([[subQ2,1.0]])],"derivedFrom":subQ1}),1.0]])]});}
            var Q18;
            {var subQ0=sQuery(id+"F0.wireOp",EDGE,"E6.left");var subQ1=sQuery(id+"F0.wireOp",EDGE,"E6.top");var subQ2=makeQuery(id+"F0.imprint","INTERSECT",VERTEX,{"derivedFrom":[subQ1,subQ0]});Q18=makeQuery(id+"F0.imprint","IMPRINT",FACE,{"disambiguationData":[TD([[makeQuery(id+"F0.imprint","IMPRINT",EDGE,{"disambiguationData":[TD([[subQ2,-1.0]])],"derivedFrom":subQ1}),1.0]])]});}
            var Q19;
            {var subQ0=sQuery(id+"F0.wireOp",EDGE,"E14.MirrorCS");var subQ1=sQuery(id+"F0.wireOp",EDGE,"E6.left");var subQ2=makeQuery(id+"F0.imprint","INTERSECT",VERTEX,{"derivedFrom":[subQ1,subQ0]});Q19=makeQuery(id+"F0.imprint","IMPRINT",FACE,{"disambiguationData":[TD([[makeQuery(id+"F0.imprint","IMPRINT",EDGE,{"disambiguationData":[TD([[subQ2,-1.0]])],"derivedFrom":subQ1}),1.0]])]});}
            var Q20;
            {var subQ0=sQuery(id+"F0.wireOp",EDGE,"E14.MirrorCS");var subQ1=sQuery(id+"F0.wireOp",EDGE,"E5.right");var subQ2=makeQuery(id+"F0.imprint","INTERSECT",VERTEX,{"derivedFrom":[subQ1,subQ0]});Q20=makeQuery(id+"F0.imprint","IMPRINT",FACE,{"disambiguationData":[TD([[makeQuery(id+"F0.imprint","IMPRINT",EDGE,{"disambiguationData":[TD([[subQ2,-1.0]])],"derivedFrom":subQ1}),-1.0]])]});}
            var Q21;
            {var subQ0=sQuery(id+"F0.wireOp",EDGE,"E5.right");var subQ1=sQuery(id+"F0.wireOp",EDGE,"E5.top");var subQ2=makeQuery(id+"F0.imprint","INTERSECT",VERTEX,{"derivedFrom":[subQ1,subQ0]});Q21=makeQuery(id+"F0.imprint","IMPRINT",FACE,{"disambiguationData":[TD([[makeQuery(id+"F0.imprint","IMPRINT",EDGE,{"disambiguationData":[TD([[subQ2,1.0]])],"derivedFrom":subQ1}),1.0]])]});}
            var Q22;
            {var subQ0=sQuery(id+"F0.wireOp",EDGE,"E5.left");var subQ1=sQuery(id+"F0.wireOp",EDGE,"E5.top");var subQ2=makeQuery(id+"F0.imprint","INTERSECT",VERTEX,{"derivedFrom":[subQ1,subQ0]});Q22=makeQuery(id+"F0.imprint","IMPRINT",FACE,{"disambiguationData":[TD([[makeQuery(id+"F0.imprint","IMPRINT",EDGE,{"disambiguationData":[TD([[subQ2,-1.0]])],"derivedFrom":subQ1}),1.0]])]});}
            var Q23;
            {var subQ0=sQuery(id+"F0.wireOp",EDGE,"E14.MirrorCS");var subQ1=sQuery(id+"F0.wireOp",EDGE,"E5.left");var subQ2=makeQuery(id+"F0.imprint","INTERSECT",VERTEX,{"derivedFrom":[subQ1,subQ0]});Q23=makeQuery(id+"F0.imprint","IMPRINT",FACE,{"disambiguationData":[TD([[makeQuery(id+"F0.imprint","IMPRINT",EDGE,{"disambiguationData":[TD([[subQ2,-1.0]])],"derivedFrom":subQ1}),1.0]])]});}
            var Q24;
            {var subQ0=sQuery(id+"F0.wireOp",EDGE,"E14.MirrorCS");var subQ1=sQuery(id+"F0.wireOp",EDGE,"E4.right");var subQ2=makeQuery(id+"F0.imprint","INTERSECT",VERTEX,{"derivedFrom":[subQ1,subQ0]});Q24=makeQuery(id+"F0.imprint","IMPRINT",FACE,{"disambiguationData":[TD([[makeQuery(id+"F0.imprint","IMPRINT",EDGE,{"disambiguationData":[TD([[subQ2,-1.0]])],"derivedFrom":subQ1}),-1.0]])]});}
            var Q25;
            {var subQ0=sQuery(id+"F0.wireOp",EDGE,"E4.right");var subQ1=sQuery(id+"F0.wireOp",EDGE,"E4.top");var subQ2=makeQuery(id+"F0.imprint","INTERSECT",VERTEX,{"derivedFrom":[subQ1,subQ0]});Q25=makeQuery(id+"F0.imprint","IMPRINT",FACE,{"disambiguationData":[TD([[makeQuery(id+"F0.imprint","IMPRINT",EDGE,{"disambiguationData":[TD([[subQ2,1.0]])],"derivedFrom":subQ1}),1.0]])]});}
            var Q26;
            {var subQ0=sQuery(id+"F0.wireOp",EDGE,"E4.left");var subQ1=sQuery(id+"F0.wireOp",EDGE,"E4.top");var subQ2=makeQuery(id+"F0.imprint","INTERSECT",VERTEX,{"derivedFrom":[subQ1,subQ0]});Q26=makeQuery(id+"F0.imprint","IMPRINT",FACE,{"disambiguationData":[TD([[makeQuery(id+"F0.imprint","IMPRINT",EDGE,{"disambiguationData":[TD([[subQ2,-1.0]])],"derivedFrom":subQ1}),1.0]])]});}
            var Q27;
            {var subQ0=sQuery(id+"F0.wireOp",EDGE,"E14.MirrorCS");var subQ1=sQuery(id+"F0.wireOp",EDGE,"E4.left");var subQ2=makeQuery(id+"F0.imprint","INTERSECT",VERTEX,{"derivedFrom":[subQ1,subQ0]});Q27=makeQuery(id+"F0.imprint","IMPRINT",FACE,{"disambiguationData":[TD([[makeQuery(id+"F0.imprint","IMPRINT",EDGE,{"disambiguationData":[TD([[subQ2,-1.0]])],"derivedFrom":subQ1}),1.0]])]});}
            var Q28;
            {var subQ0=sQuery(id+"F0.wireOp",EDGE,"E14.MirrorCS");var subQ1=sQuery(id+"F0.wireOp",EDGE,"E3.right");var subQ2=makeQuery(id+"F0.imprint","INTERSECT",VERTEX,{"derivedFrom":[subQ1,subQ0]});Q28=makeQuery(id+"F0.imprint","IMPRINT",FACE,{"disambiguationData":[TD([[makeQuery(id+"F0.imprint","IMPRINT",EDGE,{"disambiguationData":[TD([[subQ2,-1.0]])],"derivedFrom":subQ1}),-1.0]])]});}
            var Q29;
            {var subQ0=sQuery(id+"F0.wireOp",EDGE,"E28");var subQ1=sQuery(id+"F0.wireOp",EDGE,"E3.right");var subQ2=makeQuery(id+"F0.imprint","INTERSECT",VERTEX,{"derivedFrom":[subQ1,subQ0]});Q29=makeQuery(id+"F0.imprint","IMPRINT",FACE,{"disambiguationData":[TD([[makeQuery(id+"F0.imprint","IMPRINT",EDGE,{"disambiguationData":[TD([[subQ2,1.0]])],"derivedFrom":subQ1}),-1.0]])]});}
            var Q30;
            {var subQ0=sQuery(id+"F0.wireOp",EDGE,"E28");var subQ1=sQuery(id+"F0.wireOp",EDGE,"E25");var subQ2=makeQuery(id+"F0.imprint","INTERSECT",VERTEX,{"derivedFrom":[subQ1,subQ0]});Q30=makeQuery(id+"F0.imprint","IMPRINT",FACE,{"disambiguationData":[TD([[makeQuery(id+"F0.imprint","IMPRINT",EDGE,{"disambiguationData":[TD([[subQ2,1.0]])],"derivedFrom":subQ1}),1.0]])]});}
            var Q31;
            {var subQ0=sQuery(id+"F0.wireOp",EDGE,"E25");var subQ1=sQuery(id+"F0.wireOp",EDGE,"E14.MirrorCS");var subQ2=makeQuery(id+"F0.imprint","INTERSECT",VERTEX,{"derivedFrom":[subQ1,subQ0]});Q31=makeQuery(id+"F0.imprint","IMPRINT",FACE,{"disambiguationData":[TD([[makeQuery(id+"F0.imprint","IMPRINT",EDGE,{"disambiguationData":[TD([[subQ2,1.0]])],"derivedFrom":subQ1}),1.0]])]});}
            extrude(context, id + "F4", {"entities" : qUnion([Q0, Q1, Q2, Q3, Q4, Q5, Q6, Q7, Q8, Q9, Q10, Q11, Q12, Q13, Q14, Q15, Q16, Q17, Q18, Q19, Q20, Q21, Q22, Q23, Q24, Q25, Q26, Q27, Q28, Q29, Q30, Q31]), "operationType" : NewBodyOperationType.ADD, "depth" : 2.67 * mm});
        }
        {
            var Q0;
            Q0=makeQuery(id+"F4.opExtrude","CAP_EDGE",EDGE,{"disambiguationData":[OSD([sQuery(id+"F0.wireOp",EDGE,"E28")])],"isStart":false});
            var Q1;
            {var subQ0=sQuery(id+"F0.wireOp",EDGE,"E14.MirrorCS");Q1=makeQuery(id+"F4.opExtrude","CAP_EDGE",EDGE,{"disambiguationData":[OSD([subQ0]),TDD([makeQuery(id+"F0.imprint","IMPRINT",EDGE,{"disambiguationData":[TD([[makeQuery(id+"F0.imprint","INTERSECT",VERTEX,{"derivedFrom":[sQuery(id+"F0.wireOp",EDGE,"E3.right"),subQ0]}),-1.0]])],"derivedFrom":subQ0})])],"isStart":false});}
            var Q2;
            Q2=makeQuery(id+"F4.opExtrude","CAP_EDGE",EDGE,{"disambiguationData":[OSD([sQuery(id+"F0.wireOp",EDGE,"E4.top")])],"isStart":false});
            var Q3;
            {var subQ0=sQuery(id+"F0.wireOp",EDGE,"E14.MirrorCS");Q3=makeQuery(id+"F4.opExtrude","CAP_EDGE",EDGE,{"disambiguationData":[OSD([subQ0]),TDD([makeQuery(id+"F0.imprint","IMPRINT",EDGE,{"disambiguationData":[TD([[makeQuery(id+"F0.imprint","INTERSECT",VERTEX,{"derivedFrom":[sQuery(id+"F0.wireOp",EDGE,"E4.left"),subQ0]}),1.0]])],"derivedFrom":subQ0})])],"isStart":false});}
            var Q4;
            {var subQ0=sQuery(id+"F0.wireOp",EDGE,"E14.MirrorCS");Q4=makeQuery(id+"F4.opExtrude","CAP_EDGE",EDGE,{"disambiguationData":[OSD([subQ0]),TDD([makeQuery(id+"F0.imprint","IMPRINT",EDGE,{"disambiguationData":[TD([[makeQuery(id+"F0.imprint","INTERSECT",VERTEX,{"derivedFrom":[sQuery(id+"F0.wireOp",EDGE,"E5.left"),subQ0]}),1.0]])],"derivedFrom":subQ0})])],"isStart":false});}
            var Q5;
            Q5=makeQuery(id+"F4.opExtrude","CAP_EDGE",EDGE,{"disambiguationData":[OSD([sQuery(id+"F0.wireOp",EDGE,"E5.top")])],"isStart":false});
            var Q6;
            Q6=makeQuery(id+"F4.opExtrude","CAP_EDGE",EDGE,{"disambiguationData":[OSD([sQuery(id+"F0.wireOp",EDGE,"E6.top")])],"isStart":false});
            var Q7;
            {var subQ0=sQuery(id+"F0.wireOp",EDGE,"E14.MirrorCS");Q7=makeQuery(id+"F4.opExtrude","CAP_EDGE",EDGE,{"disambiguationData":[OSD([subQ0]),TDD([makeQuery(id+"F0.imprint","IMPRINT",EDGE,{"disambiguationData":[TD([[makeQuery(id+"F0.imprint","INTERSECT",VERTEX,{"derivedFrom":[sQuery(id+"F0.wireOp",EDGE,"E6.left"),subQ0]}),1.0]])],"derivedFrom":subQ0})])],"isStart":false});}
            var Q8;
            Q8=makeQuery(id+"F4.opExtrude","CAP_EDGE",EDGE,{"disambiguationData":[OSD([sQuery(id+"F0.wireOp",EDGE,"E19.MirrorCS")])],"isStart":false});
            var Q9;
            Q9=makeQuery(id+"F4.opExtrude","CAP_EDGE",EDGE,{"disambiguationData":[OSD([sQuery(id+"F0.wireOp",EDGE,"E20.MirrorCS")])],"isStart":false});
            var Q10;
            Q10=makeQuery(id+"F4.opExtrude","CAP_EDGE",EDGE,{"disambiguationData":[OSD([sQuery(id+"F0.wireOp",EDGE,"E16.MirrorCS")])],"isStart":false});
            var Q11;
            {var subQ0=sQuery(id+"F0.wireOp",EDGE,"E14.MirrorCS");Q11=makeQuery(id+"F4.opExtrude","CAP_EDGE",EDGE,{"disambiguationData":[OSD([subQ0]),TDD([makeQuery(id+"F0.imprint","IMPRINT",EDGE,{"disambiguationData":[TD([[makeQuery(id+"F0.imprint","INTERSECT",VERTEX,{"derivedFrom":[subQ0,sQuery(id+"F0.wireOp",EDGE,"E15.MirrorCS")]}),-1.0]])],"derivedFrom":subQ0})])],"isStart":false});}
            var Q12;
            {var subQ0=sQuery(id+"F0.wireOp",EDGE,"E14.MirrorCS");Q12=makeQuery(id+"F4.opExtrude","CAP_EDGE",EDGE,{"disambiguationData":[OSD([subQ0]),TDD([makeQuery(id+"F0.imprint","IMPRINT",EDGE,{"disambiguationData":[TD([[makeQuery(id+"F0.imprint","INTERSECT",VERTEX,{"derivedFrom":[sQuery(id+"F0.wireOp",EDGE,"E9.MirrorCS"),subQ0]}),1.0]])],"derivedFrom":subQ0})])],"isStart":false});}
            var Q13;
            Q13=makeQuery(id+"F4.opExtrude","CAP_EDGE",EDGE,{"disambiguationData":[OSD([sQuery(id+"F0.wireOp",EDGE,"E8.MirrorCS")])],"isStart":false});
            var Q14;
            Q14=makeQuery(id+"F4.opExtrude","CAP_EDGE",EDGE,{"disambiguationData":[OSD([sQuery(id+"F0.wireOp",EDGE,"E27")])],"isStart":false});
            var Q15;
            {var subQ0=sQuery(id+"F0.wireOp",EDGE,"E14.MirrorCS");Q15=makeQuery(id+"F4.opExtrude","CAP_EDGE",EDGE,{"disambiguationData":[OSD([subQ0]),TDD([makeQuery(id+"F0.imprint","IMPRINT",EDGE,{"disambiguationData":[TD([[makeQuery(id+"F0.imprint","INTERSECT",VERTEX,{"derivedFrom":[sQuery(id+"F0.wireOp",EDGE,"E12.MirrorCS"),subQ0]}),1.0]])],"derivedFrom":subQ0})])],"isStart":false});}
            var Q16;
            Q16=makeQuery(id+"F4.opExtrude","CAP_EDGE",EDGE,{"disambiguationData":[OSD([sQuery(id+"F0.wireOp",EDGE,"E25")])],"isStart":false});
            var Q17;
            Q17=makeQuery(id+"F4.opExtrude","CAP_EDGE",EDGE,{"disambiguationData":[OSD([sQuery(id+"F0.wireOp",EDGE,"E3.right")])],"isStart":false});
            var Q18;
            Q18=makeQuery(id+"F4.opExtrude","CAP_EDGE",EDGE,{"disambiguationData":[OSD([sQuery(id+"F0.wireOp",EDGE,"E4.left")])],"isStart":false});
            var Q19;
            Q19=makeQuery(id+"F4.opExtrude","CAP_EDGE",EDGE,{"disambiguationData":[OSD([sQuery(id+"F0.wireOp",EDGE,"E4.right")])],"isStart":false});
            var Q20;
            Q20=makeQuery(id+"F4.opExtrude","CAP_EDGE",EDGE,{"disambiguationData":[OSD([sQuery(id+"F0.wireOp",EDGE,"E5.left")])],"isStart":false});
            var Q21;
            Q21=makeQuery(id+"F4.opExtrude","CAP_EDGE",EDGE,{"disambiguationData":[OSD([sQuery(id+"F0.wireOp",EDGE,"E5.right")])],"isStart":false});
            var Q22;
            Q22=makeQuery(id+"F4.opExtrude","CAP_EDGE",EDGE,{"disambiguationData":[OSD([sQuery(id+"F0.wireOp",EDGE,"E6.left")])],"isStart":false});
            var Q23;
            Q23=makeQuery(id+"F4.opExtrude","CAP_EDGE",EDGE,{"disambiguationData":[OSD([sQuery(id+"F0.wireOp",EDGE,"E6.right")])],"isStart":false});
            var Q24;
            Q24=makeQuery(id+"F4.opExtrude","CAP_EDGE",EDGE,{"disambiguationData":[OSD([sQuery(id+"F0.wireOp",EDGE,"E21.MirrorCS")])],"isStart":false});
            var Q25;
            Q25=makeQuery(id+"F4.opExtrude","CAP_EDGE",EDGE,{"disambiguationData":[OSD([sQuery(id+"F0.wireOp",EDGE,"E18.MirrorCS")])],"isStart":false});
            var Q26;
            Q26=makeQuery(id+"F4.opExtrude","CAP_EDGE",EDGE,{"disambiguationData":[OSD([sQuery(id+"F0.wireOp",EDGE,"E17.MirrorCS")])],"isStart":false});
            var Q27;
            Q27=makeQuery(id+"F4.opExtrude","CAP_EDGE",EDGE,{"disambiguationData":[OSD([sQuery(id+"F0.wireOp",EDGE,"E15.MirrorCS")])],"isStart":false});
            var Q28;
            Q28=makeQuery(id+"F4.opExtrude","CAP_EDGE",EDGE,{"disambiguationData":[OSD([sQuery(id+"F0.wireOp",EDGE,"E9.MirrorCS")])],"isStart":false});
            var Q29;
            Q29=makeQuery(id+"F4.opExtrude","CAP_EDGE",EDGE,{"disambiguationData":[OSD([sQuery(id+"F0.wireOp",EDGE,"E10.MirrorCS")])],"isStart":false});
            var Q30;
            Q30=makeQuery(id+"F4.opExtrude","CAP_EDGE",EDGE,{"disambiguationData":[OSD([sQuery(id+"F0.wireOp",EDGE,"E12.MirrorCS")])],"isStart":false});
            var Q31;
            Q31=makeQuery(id+"F4.opExtrude","CAP_EDGE",EDGE,{"disambiguationData":[OSD([sQuery(id+"F0.wireOp",EDGE,"E26.MirrorCS")])],"isStart":false});
            chamfer(context, id + "F5", {"entities" : qUnion([Q0, Q1, Q2, Q3, Q4, Q5, Q6, Q7, Q8, Q9, Q10, Q11, Q12, Q13, Q14, Q15, Q16, Q17, Q18, Q19, Q20, Q21, Q22, Q23, Q24, Q25, Q26, Q27, Q28, Q29, Q30, Q31]), "width" : 0.25 * mm, "tangentPropagation" : true});
        }
        {
            var Q0;
            Q0=makeQuery(id+"F4.boolean.opBoolean","SPLIT",FACE,{"disambiguationData":[TD([makeQuery(id+"F4.opExtrude","SWEPT_FACE",FACE,{"disambiguationData":[OSD([sQuery(id+"F0.wireOp",EDGE,"E29")])]})])],"derivedFrom":makeQuery(id+"F1.opExtrude","CAP_FACE",FACE,{"disambiguationData":[OSD([sQuery(id+"F0.wireOp",EDGE,"E0.bottom"),sQuery(id+"F0.wireOp",EDGE,"E0.top"),sQuery(id+"F0.wireOp",EDGE,"E0.left"),sQuery(id+"F0.wireOp",EDGE,"E0.right"),sQuery(id+"F0.wireOp",EDGE,"E1"),sQuery(id+"F0.wireOp",EDGE,"E7.MirrorC"),sQuery(id+"F0.wireOp",EDGE,"E3.left")])],"isStart":false})});
            var Q1;
            Q1=makeQuery(id+"F4.boolean.opBoolean","SPLIT",FACE,{"disambiguationData":[TD([makeQuery(id+"F4.opExtrude","SWEPT_FACE",FACE,{"disambiguationData":[OSD([sQuery(id+"F0.wireOp",EDGE,"E30")])]})])],"derivedFrom":makeQuery(id+"F1.opExtrude","CAP_FACE",FACE,{"disambiguationData":[OSD([sQuery(id+"F0.wireOp",EDGE,"E0.bottom"),sQuery(id+"F0.wireOp",EDGE,"E0.top"),sQuery(id+"F0.wireOp",EDGE,"E0.left"),sQuery(id+"F0.wireOp",EDGE,"E0.right"),sQuery(id+"F0.wireOp",EDGE,"E1"),sQuery(id+"F0.wireOp",EDGE,"E7.MirrorC"),sQuery(id+"F0.wireOp",EDGE,"E3.left")])],"isStart":false})});
            var Q2;
            Q2=makeQuery(id+"F4.boolean.opBoolean","SPLIT",FACE,{"disambiguationData":[TD([makeQuery(id+"F4.opExtrude","SWEPT_FACE",FACE,{"disambiguationData":[OSD([sQuery(id+"F0.wireOp",EDGE,"E31")])]})])],"derivedFrom":makeQuery(id+"F1.opExtrude","CAP_FACE",FACE,{"disambiguationData":[OSD([sQuery(id+"F0.wireOp",EDGE,"E0.bottom"),sQuery(id+"F0.wireOp",EDGE,"E0.top"),sQuery(id+"F0.wireOp",EDGE,"E0.left"),sQuery(id+"F0.wireOp",EDGE,"E0.right"),sQuery(id+"F0.wireOp",EDGE,"E1"),sQuery(id+"F0.wireOp",EDGE,"E7.MirrorC"),sQuery(id+"F0.wireOp",EDGE,"E3.left")])],"isStart":false})});
            var Q3;
            Q3=makeQuery(id+"F4.boolean.opBoolean","SPLIT",FACE,{"disambiguationData":[TD([makeQuery(id+"F4.opExtrude","SWEPT_FACE",FACE,{"disambiguationData":[OSD([sQuery(id+"F0.wireOp",EDGE,"E32")])]})])],"derivedFrom":makeQuery(id+"F1.opExtrude","CAP_FACE",FACE,{"disambiguationData":[OSD([sQuery(id+"F0.wireOp",EDGE,"E0.bottom"),sQuery(id+"F0.wireOp",EDGE,"E0.top"),sQuery(id+"F0.wireOp",EDGE,"E0.left"),sQuery(id+"F0.wireOp",EDGE,"E0.right"),sQuery(id+"F0.wireOp",EDGE,"E1"),sQuery(id+"F0.wireOp",EDGE,"E7.MirrorC"),sQuery(id+"F0.wireOp",EDGE,"E3.left")])],"isStart":false})});
            var Q4;
            Q4=makeQuery(id+"F4.boolean.opBoolean","SPLIT",FACE,{"disambiguationData":[TD([makeQuery(id+"F4.opExtrude","SWEPT_FACE",FACE,{"disambiguationData":[OSD([sQuery(id+"F0.wireOp",EDGE,"E33.MirrorC")])]})])],"derivedFrom":makeQuery(id+"F1.opExtrude","CAP_FACE",FACE,{"disambiguationData":[OSD([sQuery(id+"F0.wireOp",EDGE,"E0.bottom"),sQuery(id+"F0.wireOp",EDGE,"E0.top"),sQuery(id+"F0.wireOp",EDGE,"E0.left"),sQuery(id+"F0.wireOp",EDGE,"E0.right"),sQuery(id+"F0.wireOp",EDGE,"E1"),sQuery(id+"F0.wireOp",EDGE,"E7.MirrorC"),sQuery(id+"F0.wireOp",EDGE,"E3.left")])],"isStart":false})});
            var Q5;
            Q5=makeQuery(id+"F4.boolean.opBoolean","SPLIT",FACE,{"disambiguationData":[TD([makeQuery(id+"F4.opExtrude","SWEPT_FACE",FACE,{"disambiguationData":[OSD([sQuery(id+"F0.wireOp",EDGE,"E34.MirrorC")])]})])],"derivedFrom":makeQuery(id+"F1.opExtrude","CAP_FACE",FACE,{"disambiguationData":[OSD([sQuery(id+"F0.wireOp",EDGE,"E0.bottom"),sQuery(id+"F0.wireOp",EDGE,"E0.top"),sQuery(id+"F0.wireOp",EDGE,"E0.left"),sQuery(id+"F0.wireOp",EDGE,"E0.right"),sQuery(id+"F0.wireOp",EDGE,"E1"),sQuery(id+"F0.wireOp",EDGE,"E7.MirrorC"),sQuery(id+"F0.wireOp",EDGE,"E3.left")])],"isStart":false})});
            var Q6;
            Q6=makeQuery(id+"F4.boolean.opBoolean","SPLIT",FACE,{"disambiguationData":[TD([makeQuery(id+"F4.opExtrude","SWEPT_FACE",FACE,{"disambiguationData":[OSD([sQuery(id+"F0.wireOp",EDGE,"E35.MirrorC")])]})])],"derivedFrom":makeQuery(id+"F1.opExtrude","CAP_FACE",FACE,{"disambiguationData":[OSD([sQuery(id+"F0.wireOp",EDGE,"E0.bottom"),sQuery(id+"F0.wireOp",EDGE,"E0.top"),sQuery(id+"F0.wireOp",EDGE,"E0.left"),sQuery(id+"F0.wireOp",EDGE,"E0.right"),sQuery(id+"F0.wireOp",EDGE,"E1"),sQuery(id+"F0.wireOp",EDGE,"E7.MirrorC"),sQuery(id+"F0.wireOp",EDGE,"E3.left")])],"isStart":false})});
            var Q7;
            Q7=makeQuery(id+"F4.boolean.opBoolean","SPLIT",FACE,{"disambiguationData":[TD([makeQuery(id+"F4.opExtrude","SWEPT_FACE",FACE,{"disambiguationData":[OSD([sQuery(id+"F0.wireOp",EDGE,"E36.MirrorC")])]})])],"derivedFrom":makeQuery(id+"F1.opExtrude","CAP_FACE",FACE,{"disambiguationData":[OSD([sQuery(id+"F0.wireOp",EDGE,"E0.bottom"),sQuery(id+"F0.wireOp",EDGE,"E0.top"),sQuery(id+"F0.wireOp",EDGE,"E0.left"),sQuery(id+"F0.wireOp",EDGE,"E0.right"),sQuery(id+"F0.wireOp",EDGE,"E1"),sQuery(id+"F0.wireOp",EDGE,"E7.MirrorC"),sQuery(id+"F0.wireOp",EDGE,"E3.left")])],"isStart":false})});
            extrude(context, id + "F6", {"entities" : qUnion([Q0, Q1, Q2, Q3, Q4, Q5, Q6, Q7]), "operationType" : NewBodyOperationType.ADD, "depth" : 1.78 * mm});
        }
    });
